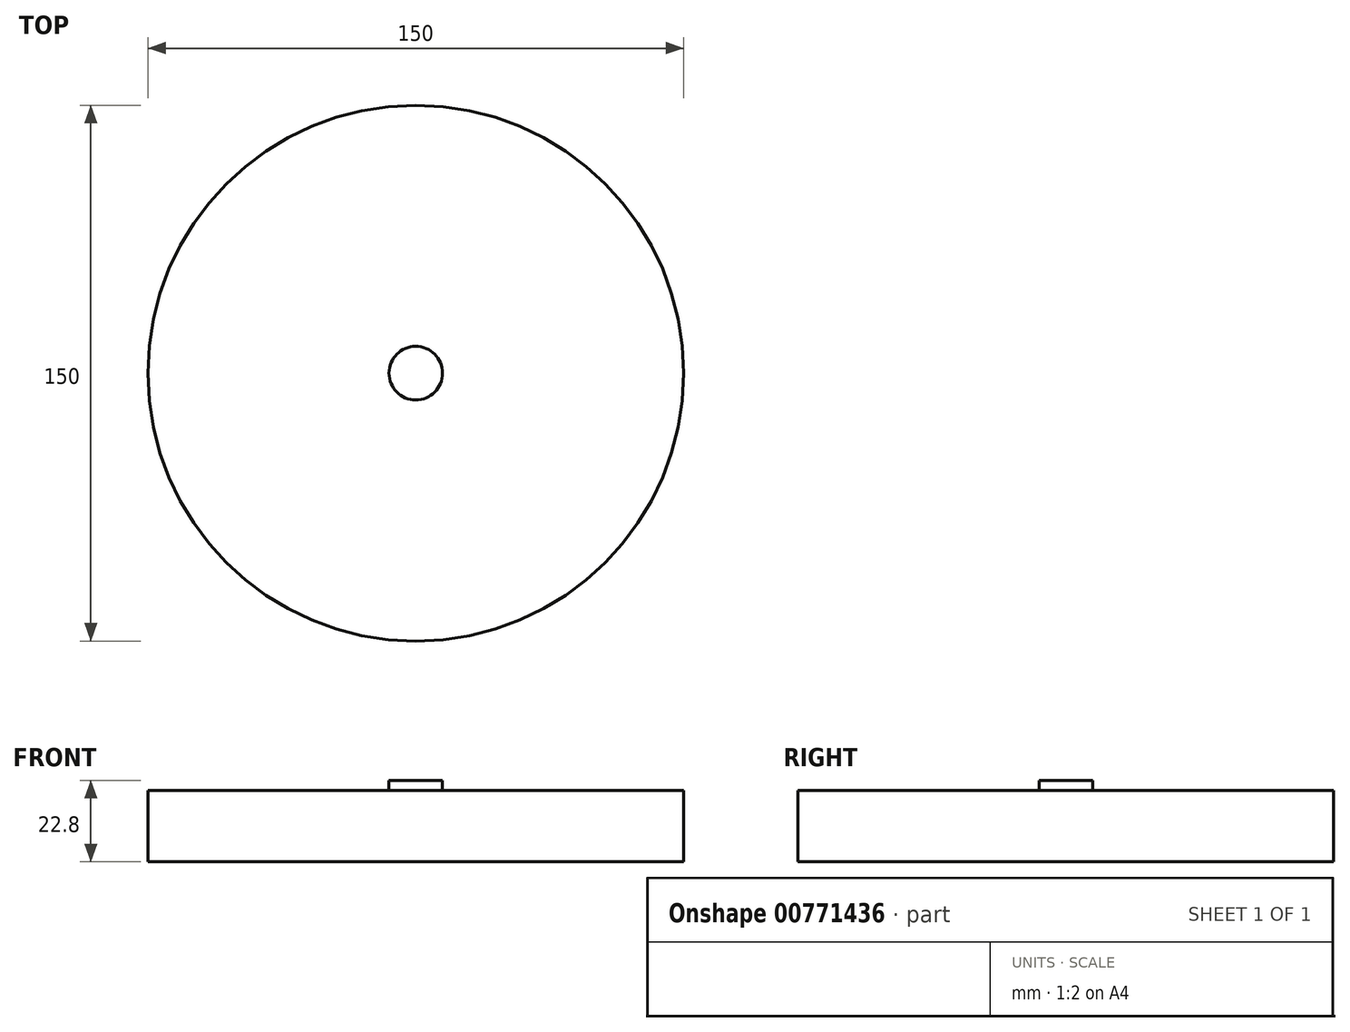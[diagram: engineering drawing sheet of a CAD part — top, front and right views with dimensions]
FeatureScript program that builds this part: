
annotation { "Feature Type Name" : "Feature", "Feature Type Description" : "" }
export const myFeature = defineFeature(function(context is Context, id is Id, definition is map)
    precondition{}
    {
        {
            var Q0;
            Q0=qCreatedBy(makeId("Top.planeOp"),FACE);
            var sketch = newSketch(context, id + "F0", { "sketchPlane" : qUnion([Q0])});
            skCircle(sketch, "E0", {"center": v(0, 0) * mm, "radius": 75 * mm});
            skSolve(sketch);
        }
        {
            var Q0;
            Q0=makeQuery(id+"F0.imprint","IMPRINT",FACE,{"disambiguationData":[TD([[makeQuery(id+"F0.imprint","IMPRINT",EDGE,{"derivedFrom":sQuery(id+"F0.wireOp",EDGE,"E0")}),1.0]])]});
            extrude(context, id + "F1", {"entities" : qUnion([Q0]), "depth" : 20 * mm, "offsetDistance" : 25 * mm});
        }
        {
            var Q0;
            Q0=makeQuery(id+"F1.opExtrude","CAP_FACE",FACE,{"disambiguationData":[OSD([sQuery(id+"F0.wireOp",EDGE,"E0")])],"isStart":false});
            var sketch = newSketch(context, id + "F2", { "sketchPlane" : qUnion([Q0])});
            skPoint(sketch, "E1", {"position": v(0, 0) * mm});
            skLineSegment(sketch, "E2.bottom", {"start": v(75, -75) * mm, "end": v(-75, -75) * mm});
            skLineSegment(sketch, "E2.top", {"start": v(75, 75) * mm, "end": v(-75, 75) * mm});
            skLineSegment(sketch, "E2.left", {"start": v(75, -75) * mm, "end": v(75, 75) * mm});
            skLineSegment(sketch, "E2.right", {"start": v(-75, -75) * mm, "end": v(-75, 75) * mm});
            skLineSegment(sketch, "E3", {"start": v(-75, -75) * mm, "end": v(75, 75) * mm});
            skLineSegment(sketch, "E4", {"start": v(-75, 75) * mm, "end": v(75, -75) * mm});
            skLineSegment(sketch, "E5", {"start": v(75, 0) * mm, "end": v(-75, 0) * mm});
            skLineSegment(sketch, "E6", {"start": v(0, 75) * mm, "end": v(0, -75) * mm});
            skLineSegment(sketch, "E7", {"start": v(0, 0) * mm, "end": v(53.03, -53.03) * mm});
            skLineSegment(sketch, "E8", {"start": v(53.03, -53.03) * mm, "end": v(0, -75) * mm});
            skPoint(sketch, "E9", {"position": v(26.52, -64.02) * mm});
            skLineSegment(sketch, "E10", {"start": v(26.52, -64.02) * mm, "end": v(0, 0) * mm});
            skLineSegment(sketch, "E11", {"start": v(0, 0) * mm, "end": v(-28.7, 69.3) * mm});
            skLineSegment(sketch, "E12", {"start": v(-28.7, 69.3) * mm, "end": v(28.7, -69.3) * mm});
            skLineSegment(sketch, "E13", {"start": v(53.03, -53.03) * mm, "end": v(75, 0) * mm});
            skLineSegment(sketch, "E14", {"start": v(0, 0) * mm, "end": v(-53.03, -53.03) * mm});
            skLineSegment(sketch, "E15", {"start": v(-53.03, -53.03) * mm, "end": v(53.03, 53.03) * mm});
            skLineSegment(sketch, "E16", {"start": v(53.03, 53.03) * mm, "end": v(75, 0) * mm});
            skLineSegment(sketch, "E17", {"start": v(-53.03, -53.03) * mm, "end": v(0, -75) * mm});
            skLineSegment(sketch, "E18", {"start": v(-26.52, -64.02) * mm, "end": v(28.7, 69.3) * mm});
            skLineSegment(sketch, "E19", {"start": v(64.02, 26.52) * mm, "end": v(-69.3, -28.7) * mm});
            skLineSegment(sketch, "E20", {"start": v(64.02, -26.52) * mm, "end": v(-69.3, 28.7) * mm});
            skLineSegment(sketch, "E21", {"start": v(-69.3, 28.7) * mm, "end": v(69.3, -28.7) * mm});
            skLineSegment(sketch, "E22", {"start": v(-26.52, -64.02) * mm, "end": v(-28.7, -69.3) * mm});
            skLineSegment(sketch, "E23", {"start": v(64.02, 26.52) * mm, "end": v(69.3, 28.7) * mm});
            skSolve(sketch);
        }
        {
            var Q0;
            {var subQ0=sQuery(id+"F2.wireOp",EDGE,"E19");var subQ3=makeQuery(id+"F1.opExtrude","CAP_EDGE",EDGE,{"disambiguationData":[OSD([sQuery(id+"F0.wireOp",EDGE,"E0")])],"isStart":false});var subQ5=makeQuery(id+"F2.imprint","INTERSECT",VERTEX,{"derivedFrom":[subQ3,subQ0]});Q0=makeQuery(id+"F2.imprint","IMPRINT",FACE,{"disambiguationData":[TD([[makeQuery(id+"F2.imprint","IMPRINT",EDGE,{"disambiguationData":[TD([[subQ5,-1.0]])],"derivedFrom":subQ3}),1.0]])]});}
            var sketch = newSketch(context, id + "F3", { "sketchPlane" : qUnion([Q0])});
            skCircle(sketch, "E24", {"center": v(0, 0) * mm, "radius": 7.5 * mm});
            skSolve(sketch);
        }
        {
            var Q0;
            Q0 = qSketchRegion(id + "F3", true);
            extrude(context, id + "F4", {"entities" : qUnion([Q0]), "operationType" : NewBodyOperationType.ADD, "depth" : 25 * mm, "offsetDistance" : 25 * mm});
        }
        {
            var Q0;
            Q0=makeQuery(id+"F4.opExtrude","CAP_FACE",FACE,{"disambiguationData":[OSD([sQuery(id+"F3.wireOp",EDGE,"E24")])],"isStart":false});
            extrude(context, id + "F5", {"entities" : qUnion([Q0]), "operationType" : NewBodyOperationType.REMOVE, "oppositeDirection" : true, "depth" : 22.2 * mm, "offsetDistance" : 25 * mm});
        }
    });
